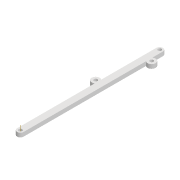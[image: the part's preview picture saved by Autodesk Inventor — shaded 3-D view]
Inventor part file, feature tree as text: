
AUTODESK INVENTOR PART (.ipt)
format: ipt  version: 2022 (Build 260153000, 153)  size: 107,008 bytes
history: native  units: mm
features: extrude x1, other x1, sketch x1
ambient origin geometry x8: Origin, YZ Plane, XZ Plane, XY Plane, X Axis, Y Axis, Z Axis, Center Point
bodies: Solid1 (feature_tree)
feature tree (3):
  extrude  "Extrusion1"  Depth=8.0mm
  other  "Work Axis1"
  sketch  "Sketch1"  dims[d0=172.0mm d1=8.0mm d2=4.2mm d3=4.2mm d4=5.0mm d5=0.0mm d8=4.2mm d9=100.0mm d10=3.0mm d11=10.0mm d12=4.2mm d13=10.0mm d15=3.0mm d16=150.0mm]
